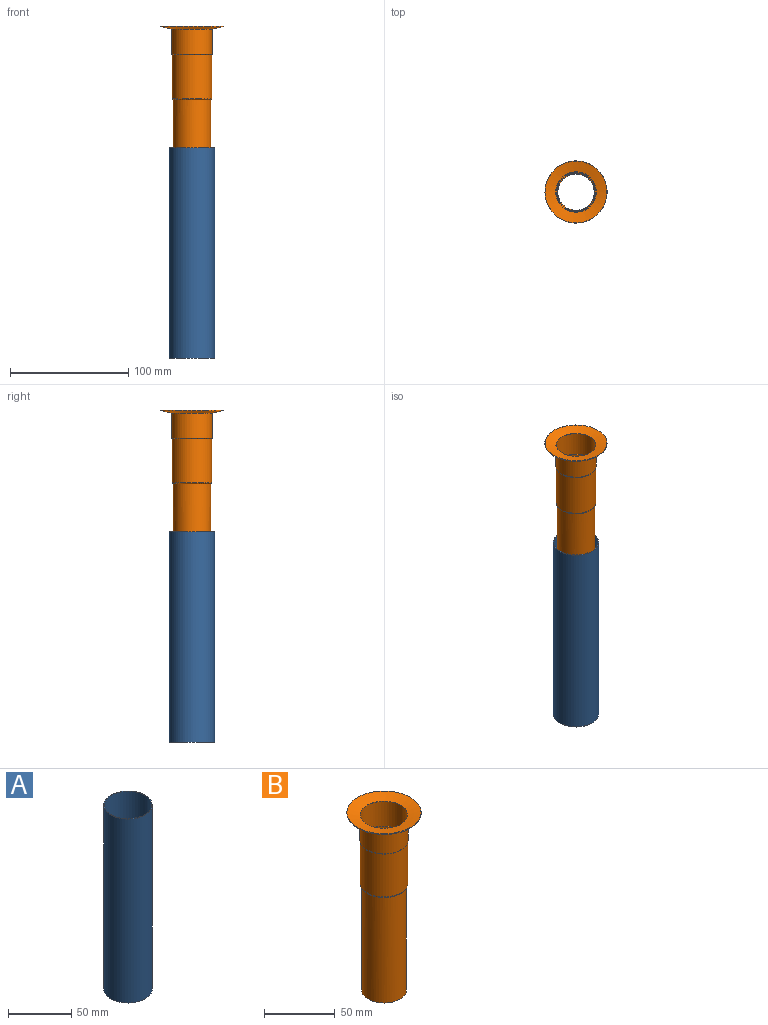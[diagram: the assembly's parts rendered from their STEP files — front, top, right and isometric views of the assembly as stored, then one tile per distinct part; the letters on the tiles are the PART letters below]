
ASSEMBLY  parts=2 mates=2
PART A: 4 faces, bbox 38.4x38.4x177.8 mm
  f0: cylinder r=18.73mm len=177.8mm, axis (0,0,-1), area 20927mm2, adj f2,f3
  f1: cylinder r=19.18mm len=177.8mm, axis (0,0,-1), area 21423.6mm2, adj f2,f3
  f2: plane 38.35x38.35mm, normal (0,0,1), area 52.9mm2, adj f0,f1
  f3: plane 38.35x38.35mm, normal (0,0,-1), area 52.9mm2, adj f0,f1
PART B: 15 faces, bbox 52.6x52.6x153.7 mm
  f0: cylinder r=15.43mm len=91.88mm, axis (0,0,-1), area 8908.4mm2, adj f2,f7
  f1: cylinder r=15.88mm len=91.44mm, axis (0,0,-1), area 9120.7mm2, adj f2,f8
  f2: plane 31.75x31.75mm, normal (0,0,-1), area 43.7mm2, adj f0,f1
  f3: cylinder r=16.64mm len=33.27mm, axis (0,0,-1), area 2254.5mm2, adj f4,f14
  f4: plane 33.27x33.27mm, normal (0,0,1), area 29mm2, adj f3,f5
  f5: cylinder r=16.36mm len=37.62mm, axis (0,0,-1), area 3866.2mm2, adj f4,f6
  f6: torus R=15.88mm, axis (0,0,-1), area 77.1mm2, adj f5,f7
  f7: plane 31.75x31.75mm, normal (0,0,1), area 43.7mm2, adj f0,f6
  f8: torus R=15.88mm, axis (0,0,-1), area 150.7mm2, adj f1,f9
  f9: cylinder r=16.8mm len=37.17mm, axis (0,0,-1), area 3924.4mm2, adj f8,f10
  f10: torus R=16.8mm, axis (0,0,-1), area 46.8mm2, adj f9,f11
  f11: cylinder r=17.08mm len=34.16mm, axis (0,0,-1), area 2287.2mm2, adj f10,f12
  f12: cone r=17.08mm half-angle=77.5deg, axis (0,0,1), area 1285.1mm2, adj f11,f13
  f13: cone r=26.29mm half-angle=12.5deg, axis (0,0,-1), area 83.7mm2, adj f12,f14
  f14: cone r=16.64mm half-angle=77.5deg, axis (0,0,1), area 1314.7mm2, adj f3,f13
PLACE A t=(0,0,-127)mm
PLACE B at identity fixed
MATE cylindrical B.f1 <-> A.f0  axis (0,0,-1) through (0,0,0)mm
MATE planar B.f1 <-> A.f0  axis (0,0,-1) through (0,0,0)mm
